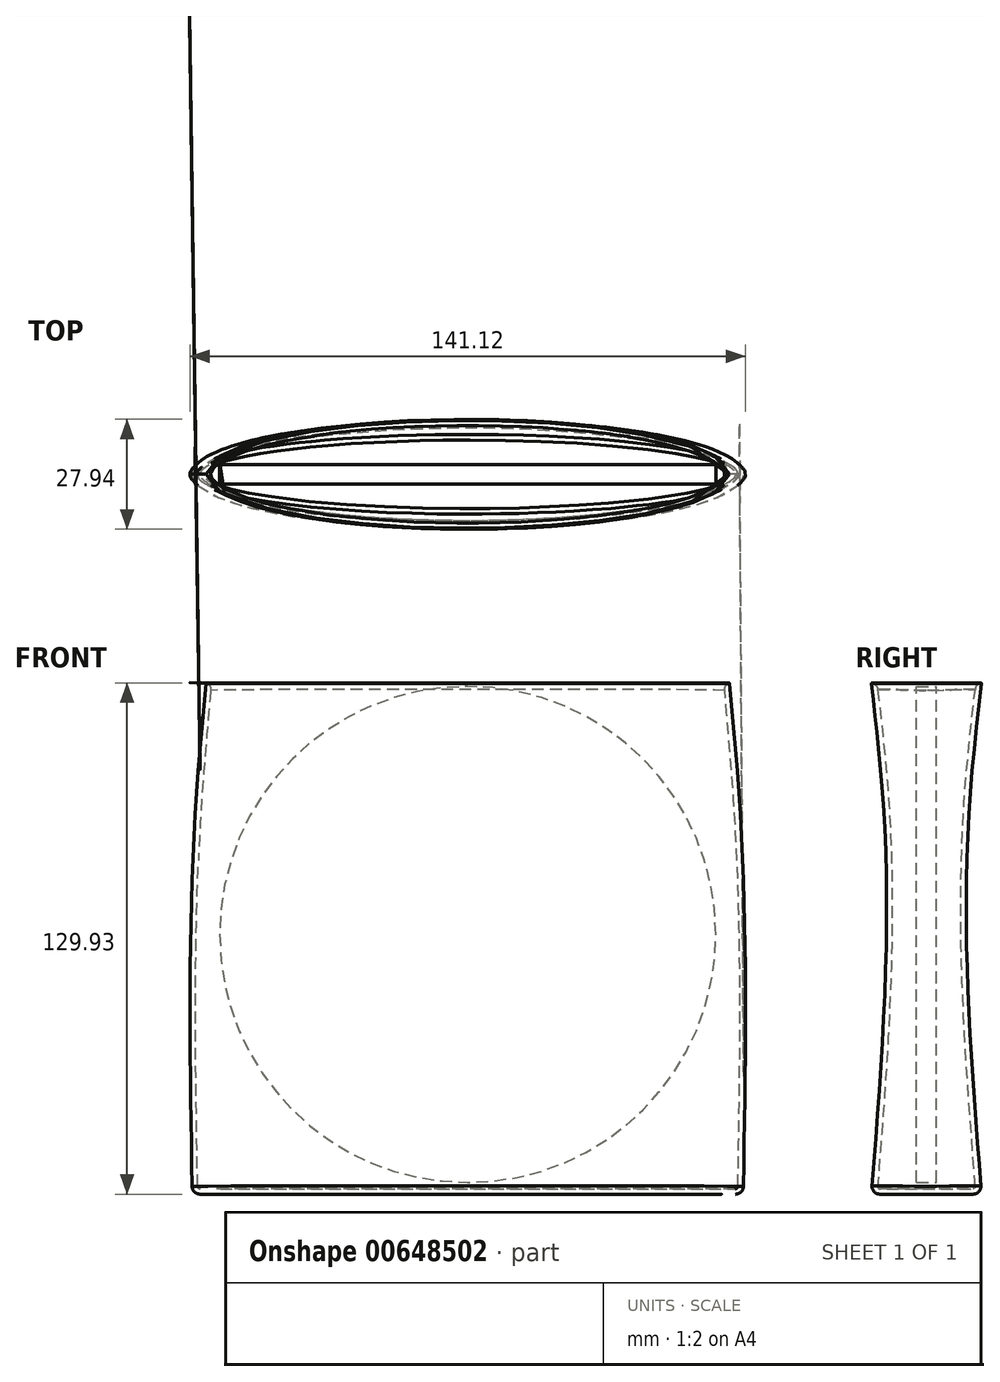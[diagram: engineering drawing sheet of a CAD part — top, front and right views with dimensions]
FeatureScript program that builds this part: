
annotation { "Feature Type Name" : "Feature", "Feature Type Description" : "" }
export const myFeature = defineFeature(function(context is Context, id is Id, definition is map)
    precondition{}
    {
        {
            var Q0;
            Q0=qCreatedBy(makeId("Top.planeOp"),FACE);
            var sketch = newSketch(context, id + "F0", { "sketchPlane" : qUnion([Q0])});
            skEllipse(sketch, "E0", {"center": v(0, 0) * mm, "majorRadius": 70 * mm, "minorRadius": 14 * mm, "majorAxis": v(-1, 0)});
            skSolve(sketch);
        }
        {
            var Q0;
            Q0=qCreatedBy(makeId("Top.planeOp"),FACE);
            cPlane(context, id + "F1", {"entities" : qUnion([Q0]), "cplaneType" : CPlaneType.OFFSET, "offset" : 100 * mm, "width" : 150 * mm, "height" : 150 * mm});
        }
        {
            var Q0;
            Q0=qCreatedBy(id+"F1.planeOp",FACE);
            var sketch = newSketch(context, id + "F2", { "sketchPlane" : qUnion([Q0])});
            skEllipse(sketch, "E1", {"center": v(0, 0) * mm, "majorRadius": 69 * mm, "minorRadius": 11 * mm, "majorAxis": v(-1, 0)});
            skSolve(sketch);
        }
        {
            var Q0;
            Q0=qCreatedBy(id+"F1.planeOp",FACE);
            cPlane(context, id + "F3", {"entities" : qUnion([Q0]), "cplaneType" : CPlaneType.OFFSET, "offset" : 30 * mm, "width" : 150 * mm, "height" : 150 * mm});
        }
        {
            var Q0;
            Q0=qCreatedBy(id+"F3.planeOp",FACE);
            var sketch = newSketch(context, id + "F4", { "sketchPlane" : qUnion([Q0])});
            skEllipse(sketch, "E2.0", {"center": v(0, 0) * mm, "majorRadius": 66.5 * mm, "minorRadius": 14 * mm, "majorAxis": v(-1, 0)});
            skSolve(sketch);
        }
        {
            var Q0;
            Q0=qCreatedBy(makeId("Front.planeOp"),FACE);
            var sketch = newSketch(context, id + "F5", { "sketchPlane" : qUnion([Q0])});
            skCircle(sketch, "E3", {"center": v(0, 66) * mm, "radius": 63 * mm});
            skSolve(sketch);
        }
        {
            var Q0;
            Q0=makeQuery(id+"F5.imprint","IMPRINT",FACE,{"disambiguationData":[TD([[makeQuery(id+"F5.imprint","IMPRINT",EDGE,{"derivedFrom":sQuery(id+"F5.wireOp",EDGE,"E3")}),1.0]])]});
            extrude(context, id + "F6", {"entities" : qUnion([Q0]), "endBound" : BoundingType.SYMMETRIC, "depth" : 5 * mm, "offsetDistance" : 25 * mm});
        }
        {
            var Q0;
            Q0=makeQuery(id+"F0.imprint","IMPRINT",FACE,{"disambiguationData":[TD([[makeQuery(id+"F0.imprint","IMPRINT",EDGE,{"derivedFrom":sQuery(id+"F0.wireOp",EDGE,"E0")}),1.0]])]});
            var Q1;
            Q1=makeQuery(id+"F2.imprint","IMPRINT",FACE,{"disambiguationData":[TD([[makeQuery(id+"F2.imprint","IMPRINT",EDGE,{"derivedFrom":sQuery(id+"F2.wireOp",EDGE,"E1")}),1.0]])]});
            var Q2;
            Q2=makeQuery(id+"F4.imprint","IMPRINT",FACE,{"disambiguationData":[TD([[makeQuery(id+"F4.imprint","IMPRINT",EDGE,{"derivedFrom":sQuery(id+"F4.wireOp",EDGE,"E2.0")}),1.0]])]});
            loft(context, id + "F7", {"sheetProfilesArray" : [{ "sheetProfileEntities" : qUnion([Q0]) }, { "sheetProfileEntities" : qUnion([Q1]) }, { "sheetProfileEntities" : qUnion([Q2]) }]});
        }
        {
            var Q0;
            Q0=makeQuery(id+"F7.opLoft","MID_CAP_EDGE",EDGE,{"disambiguationData":[OSD([sQuery(id+"F0.wireOp",EDGE,"E0")])],"capPos":0.0});
            fillet(context, id + "F8", {"entities" : qUnion([Q0]), "radius" : 2 * mm, "tangentPropagation" : true, "allowEdgeOverflow" : false});
        }
        {
            var Q0;
            Q0=makeQuery(id+"F7.opLoft","CAP_FACE",FACE,{"disambiguationData":[OSD([makeQuery(id+"F4.imprint","IMPRINT",FACE,{"disambiguationData":[TD([[makeQuery(id+"F4.imprint","IMPRINT",EDGE,{"derivedFrom":sQuery(id+"F4.wireOp",EDGE,"E2.0")}),1.0]])]})])],"isStart":true});
            shell(context, id + "F9", {"entities" : qUnion([Q0]), "thickness" : 1.4 * mm});
        }
        {
            var Q0;
            Q0=makeQuery(id+"F9.opShell","OFFSET_EDGE",EDGE,{"disambiguationData":[OSD([sQuery(id+"F4.wireOp",EDGE,"E2.0")])]});
            fillet(context, id + "F10", {"entities" : qUnion([Q0]), "radius" : 2 * mm, "tangentPropagation" : true, "allowEdgeOverflow" : false});
        }
        {
            var Q0;
            {var subQ0=sQuery(id+"F4.wireOp",EDGE,"E2.0");Q0=makeQuery(id+"F10.opFillet","BLEND_EDGE",EDGE,{"blendedFrom":[makeQuery(id+"F9.opShell","OFFSET_EDGE",EDGE,{"disambiguationData":[OSD([subQ0])]}),makeQuery(id+"F7.opLoft","SWEPT_FACE",FACE,{"disambiguationData":[OSD([sQuery(id+"F0.wireOp",EDGE,"E0"),sQuery(id+"F2.wireOp",EDGE,"E1"),subQ0])]})],"blendedInto":[makeQuery(id+"F7.opLoft","SWEPT_FACE",FACE,{"disambiguationData":[OSD([sQuery(id+"F0.wireOp",EDGE,"E0"),sQuery(id+"F2.wireOp",EDGE,"E1"),subQ0])]})]});}
            fillet(context, id + "F11", {"entities" : qUnion([Q0]), "radius" : .2 * mm, "tangentPropagation" : true, "allowEdgeOverflow" : false});
        }
    });
